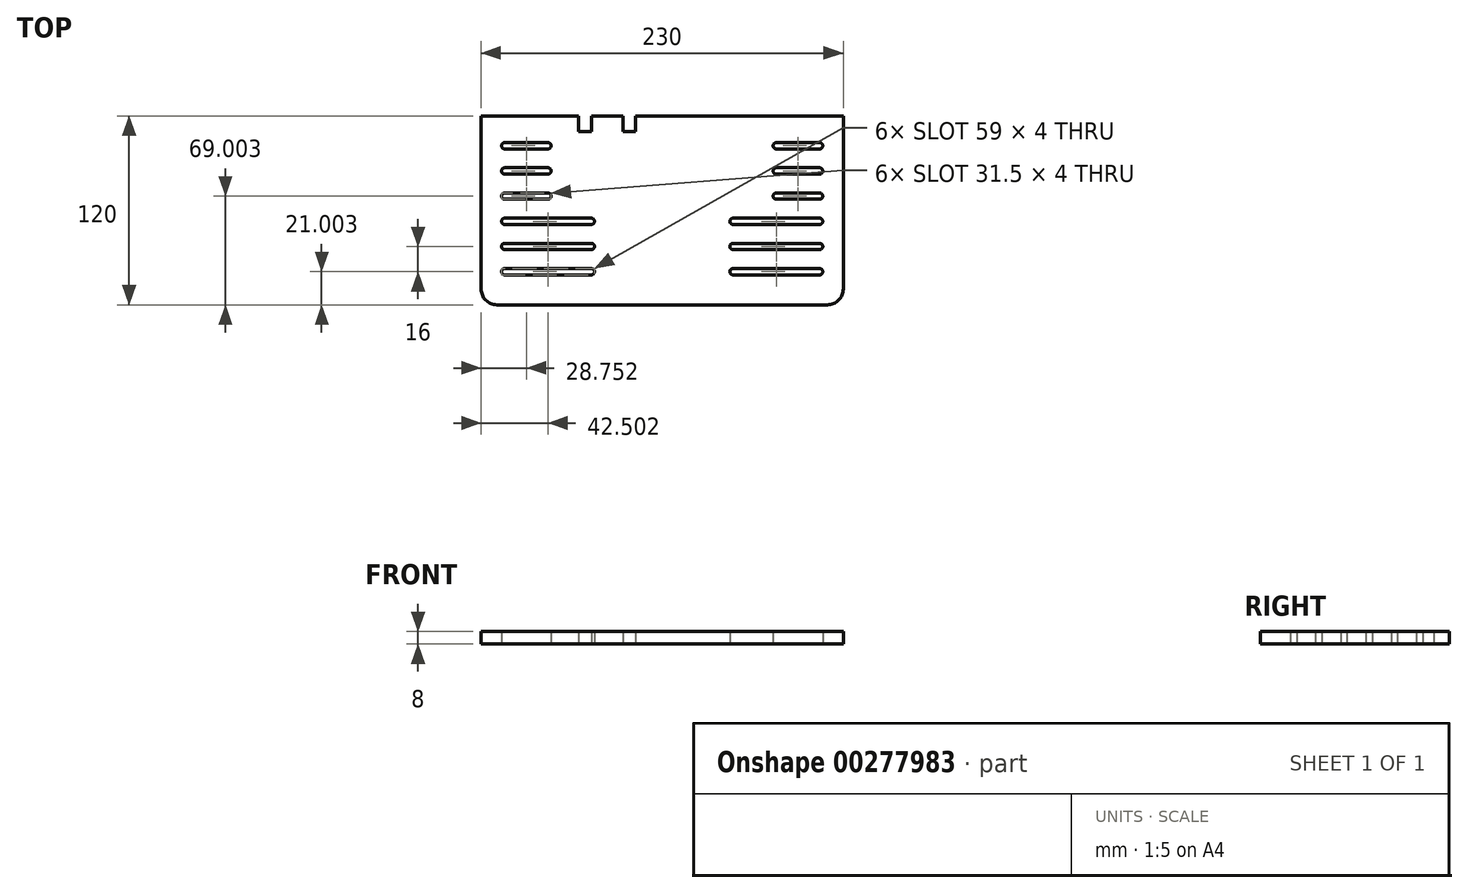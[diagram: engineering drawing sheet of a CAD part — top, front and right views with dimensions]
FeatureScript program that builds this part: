
annotation { "Feature Type Name" : "Feature", "Feature Type Description" : "" }
export const myFeature = defineFeature(function(context is Context, id is Id, definition is map)
    precondition{}
    {
        {
            var Q0;
            Q0=qCreatedBy(makeId("Top.planeOp"),FACE);
            var sketch = newSketch(context, id + "F0", { "sketchPlane" : qUnion([Q0])});
            skLineSegment(sketch, "E0", {"start": v(-45.56, -13.54) * mm, "end": v(16.44, -13.54) * mm});
            skLineSegment(sketch, "E1", {"start": v(16.44, -13.54) * mm, "end": v(16.44, -23.54) * mm});
            skLineSegment(sketch, "E2", {"start": v(16.44, -23.54) * mm, "end": v(24.44, -23.54) * mm});
            skLineSegment(sketch, "E3", {"start": v(24.44, -23.54) * mm, "end": v(24.44, -13.54) * mm});
            skLineSegment(sketch, "E4", {"start": v(24.44, -13.54) * mm, "end": v(44.44, -13.54) * mm});
            skLineSegment(sketch, "E5", {"start": v(44.44, -13.54) * mm, "end": v(44.44, -23.54) * mm});
            skLineSegment(sketch, "E6", {"start": v(44.44, -23.54) * mm, "end": v(52.44, -23.54) * mm});
            skLineSegment(sketch, "E7", {"start": v(52.44, -23.54) * mm, "end": v(52.44, -13.54) * mm});
            skLineSegment(sketch, "E8", {"start": v(184.44, -13.54) * mm, "end": v(184.44, -133.54) * mm});
            skLineSegment(sketch, "E9", {"start": v(184.44, -133.54) * mm, "end": v(-45.56, -133.54) * mm});
            skLineSegment(sketch, "E10", {"start": v(-45.56, -133.54) * mm, "end": v(-45.56, -13.54) * mm});
            skLineSegment(sketch, "E11", {"start": v(52.44, -13.54) * mm, "end": v(184.44, -13.54) * mm});
            skLineSegment(sketch, "E12.0", {"start": v(-30.56, -80.54) * mm, "end": v(24.44, -80.54) * mm});
            skArc(sketch, "E13.3.startCap", {"start": v(-30.56, -82.54) * mm, "mid": v(-32.56, -80.54) * mm, "end": v(-30.56, -78.54) * mm});
            skArc(sketch, "E13.3.endCap", {"start": v(24.44, -78.54) * mm, "mid": v(26.44, -80.54) * mm, "end": v(24.44, -82.54) * mm});
            skLineSegment(sketch, "E13.3.left", {"start": v(-30.56, -78.54) * mm, "end": v(24.44, -78.54) * mm});
            skLineSegment(sketch, "E13.3.right", {"start": v(-30.56, -82.54) * mm, "end": v(24.44, -82.54) * mm});
            skLineSegment(sketch, "E14.0.1.0", {"start": v(-30.56, -94.54) * mm, "end": v(24.44, -94.54) * mm});
            skLineSegment(sketch, "E14.0.1.1", {"start": v(-30.56, -96.54) * mm, "end": v(24.44, -96.54) * mm});
            skLineSegment(sketch, "E14.0.1.2", {"start": v(-30.56, -98.54) * mm, "end": v(24.44, -98.54) * mm});
            skArc(sketch, "E14.0.1.3", {"start": v(-30.56, -98.54) * mm, "mid": v(-32.56, -96.54) * mm, "end": v(-30.56, -94.54) * mm});
            skArc(sketch, "E14.0.1.4", {"start": v(24.44, -94.54) * mm, "mid": v(26.44, -96.54) * mm, "end": v(24.44, -98.54) * mm});
            skLineSegment(sketch, "E14.direction1", {"start": v(-30.56, -82.54) * mm, "end": v(-5.56, -82.54) * mm, "construction": true});
            skLineSegment(sketch, "E14.direction2", {"start": v(-30.56, -82.54) * mm, "end": v(-30.56, -98.54) * mm, "construction": true});
            skLineSegment(sketch, "E15.0.0.2", {"start": v(-30.56, -110.54) * mm, "end": v(24.44, -110.54) * mm});
            skLineSegment(sketch, "E15.3.0.2", {"start": v(-30.56, -112.54) * mm, "end": v(24.44, -112.54) * mm});
            skLineSegment(sketch, "E15.6.0.2", {"start": v(-30.56, -114.54) * mm, "end": v(24.44, -114.54) * mm});
            skArc(sketch, "E15.9.0.2", {"start": v(-30.56, -114.54) * mm, "mid": v(-32.56, -112.54) * mm, "end": v(-30.56, -110.54) * mm});
            skArc(sketch, "E15.13.0.2", {"start": v(24.44, -110.54) * mm, "mid": v(26.44, -112.54) * mm, "end": v(24.44, -114.54) * mm});
            skArc(sketch, "E16.MirrorCS", {"start": v(169.44, -82.54) * mm, "mid": v(171.44, -80.54) * mm, "end": v(169.44, -78.54) * mm});
            skArc(sketch, "E17.MirrorCS", {"start": v(169.44, -98.54) * mm, "mid": v(171.44, -96.54) * mm, "end": v(169.44, -94.54) * mm});
            skArc(sketch, "E18.MirrorCS", {"start": v(169.44, -114.54) * mm, "mid": v(171.44, -112.54) * mm, "end": v(169.44, -110.54) * mm});
            skLineSegment(sketch, "E19.MirrorCS", {"start": v(169.44, -98.54) * mm, "end": v(114.44, -98.54) * mm});
            skArc(sketch, "E20.MirrorCS", {"start": v(114.44, -110.54) * mm, "mid": v(112.44, -112.54) * mm, "end": v(114.44, -114.54) * mm});
            skLineSegment(sketch, "E21.MirrorCS", {"start": v(169.44, -110.54) * mm, "end": v(114.44, -110.54) * mm});
            skLineSegment(sketch, "E22.MirrorCS", {"start": v(169.44, -82.54) * mm, "end": v(169.44, -98.54) * mm, "construction": true});
            skLineSegment(sketch, "E23.MirrorCS", {"start": v(169.44, -82.54) * mm, "end": v(144.44, -82.54) * mm, "construction": true});
            skLineSegment(sketch, "E24.MirrorCS", {"start": v(169.44, -80.54) * mm, "end": v(114.44, -80.54) * mm});
            skLineSegment(sketch, "E25.MirrorCS", {"start": v(169.44, -114.54) * mm, "end": v(114.44, -114.54) * mm});
            skLineSegment(sketch, "E26.MirrorCS", {"start": v(169.44, -94.54) * mm, "end": v(114.44, -94.54) * mm});
            skLineSegment(sketch, "E27.MirrorCS", {"start": v(169.44, -96.54) * mm, "end": v(114.44, -96.54) * mm});
            skArc(sketch, "E28.MirrorCS", {"start": v(114.44, -94.54) * mm, "mid": v(112.44, -96.54) * mm, "end": v(114.44, -98.54) * mm});
            skArc(sketch, "E29.MirrorCS", {"start": v(114.44, -78.54) * mm, "mid": v(112.44, -80.54) * mm, "end": v(114.44, -82.54) * mm});
            skLineSegment(sketch, "E30.MirrorCS", {"start": v(169.44, -112.54) * mm, "end": v(114.44, -112.54) * mm});
            skLineSegment(sketch, "E31.MirrorCS", {"start": v(169.44, -78.54) * mm, "end": v(114.44, -78.54) * mm});
            skLineSegment(sketch, "E32.MirrorCS", {"start": v(169.44, -82.54) * mm, "end": v(114.44, -82.54) * mm});
            skLineSegment(sketch, "E33", {"start": v(-30.56, -64.54) * mm, "end": v(-3.06, -64.54) * mm});
            skLineSegment(sketch, "E34", {"start": v(-30.56, -48.54) * mm, "end": v(-3.06, -48.54) * mm});
            skLineSegment(sketch, "E35", {"start": v(-30.56, -32.54) * mm, "end": v(-3.06, -32.54) * mm});
            skArc(sketch, "E36.0.startCap", {"start": v(-30.56, -34.54) * mm, "mid": v(-32.56, -32.54) * mm, "end": v(-30.56, -30.54) * mm});
            skArc(sketch, "E36.0.endCap", {"start": v(-3.06, -30.54) * mm, "mid": v(-1.06, -32.54) * mm, "end": v(-3.06, -34.54) * mm});
            skLineSegment(sketch, "E36.0.left", {"start": v(-30.56, -30.54) * mm, "end": v(-3.06, -30.54) * mm});
            skLineSegment(sketch, "E36.0.right", {"start": v(-30.56, -34.54) * mm, "end": v(-3.06, -34.54) * mm});
            skArc(sketch, "E36.1.startCap", {"start": v(-30.56, -50.54) * mm, "mid": v(-32.56, -48.54) * mm, "end": v(-30.56, -46.54) * mm});
            skArc(sketch, "E36.1.endCap", {"start": v(-3.06, -46.54) * mm, "mid": v(-1.06, -48.54) * mm, "end": v(-3.06, -50.54) * mm});
            skLineSegment(sketch, "E36.1.left", {"start": v(-30.56, -46.54) * mm, "end": v(-3.06, -46.54) * mm});
            skLineSegment(sketch, "E36.1.right", {"start": v(-30.56, -50.54) * mm, "end": v(-3.06, -50.54) * mm});
            skArc(sketch, "E36.2.startCap", {"start": v(-30.56, -66.54) * mm, "mid": v(-32.56, -64.54) * mm, "end": v(-30.56, -62.54) * mm});
            skArc(sketch, "E36.2.endCap", {"start": v(-3.06, -62.54) * mm, "mid": v(-1.06, -64.54) * mm, "end": v(-3.06, -66.54) * mm});
            skLineSegment(sketch, "E36.2.left", {"start": v(-30.56, -62.54) * mm, "end": v(-3.06, -62.54) * mm});
            skLineSegment(sketch, "E36.2.right", {"start": v(-30.56, -66.54) * mm, "end": v(-3.06, -66.54) * mm});
            skArc(sketch, "E37.MirrorCS", {"start": v(169.44, -66.54) * mm, "mid": v(171.44, -64.54) * mm, "end": v(169.44, -62.54) * mm});
            skArc(sketch, "E38.MirrorCS", {"start": v(141.94, -62.54) * mm, "mid": v(139.94, -64.54) * mm, "end": v(141.94, -66.54) * mm});
            skArc(sketch, "E39.MirrorCS", {"start": v(169.44, -34.54) * mm, "mid": v(171.44, -32.54) * mm, "end": v(169.44, -30.54) * mm});
            skArc(sketch, "E40.MirrorCS", {"start": v(169.44, -50.54) * mm, "mid": v(171.44, -48.54) * mm, "end": v(169.44, -46.54) * mm});
            skArc(sketch, "E41.MirrorCS", {"start": v(141.94, -30.54) * mm, "mid": v(139.94, -32.54) * mm, "end": v(141.94, -34.54) * mm});
            skArc(sketch, "E42.MirrorCS", {"start": v(141.94, -46.54) * mm, "mid": v(139.94, -48.54) * mm, "end": v(141.94, -50.54) * mm});
            skLineSegment(sketch, "E43.MirrorCS", {"start": v(169.44, -32.54) * mm, "end": v(141.94, -32.54) * mm});
            skLineSegment(sketch, "E44.MirrorCS", {"start": v(169.44, -30.54) * mm, "end": v(141.94, -30.54) * mm});
            skLineSegment(sketch, "E45.MirrorCS", {"start": v(169.44, -50.54) * mm, "end": v(141.94, -50.54) * mm});
            skLineSegment(sketch, "E46.MirrorCS", {"start": v(169.44, -62.54) * mm, "end": v(141.94, -62.54) * mm});
            skLineSegment(sketch, "E47.MirrorCS", {"start": v(169.44, -48.54) * mm, "end": v(141.94, -48.54) * mm});
            skLineSegment(sketch, "E48.MirrorCS", {"start": v(169.44, -34.54) * mm, "end": v(141.94, -34.54) * mm});
            skLineSegment(sketch, "E49.MirrorCS", {"start": v(169.44, -66.54) * mm, "end": v(141.94, -66.54) * mm});
            skLineSegment(sketch, "E50.MirrorCS", {"start": v(169.44, -46.54) * mm, "end": v(141.94, -46.54) * mm});
            skLineSegment(sketch, "E51.MirrorCS", {"start": v(169.44, -64.54) * mm, "end": v(141.94, -64.54) * mm});
            skSolve(sketch);
        }
        {
            var Q0;
            Q0=qSketchRegion(id+"F0",true);
            extrude(context, id + "F1", {"entities" : qUnion([Q0]), "depth" : 8 * mm});
        }
        {
            var Q0;
            Q0=makeQuery(id+"F1.opExtrude","SWEPT_EDGE",EDGE,{"disambiguationData":[OSD([sQuery(id+"F0.wireOp",EDGE,"E9"),sQuery(id+"F0.wireOp",EDGE,"E10")])]});
            var Q1;
            Q1=makeQuery(id+"F1.opExtrude","SWEPT_EDGE",EDGE,{"disambiguationData":[OSD([sQuery(id+"F0.wireOp",EDGE,"E8"),sQuery(id+"F0.wireOp",EDGE,"E9")])]});
            fillet(context, id + "F2", {"entities" : qUnion([Q0, Q1]), "radius" : 10 * mm, "tangentPropagation" : true, "allowEdgeOverflow" : false});
        }
    });
